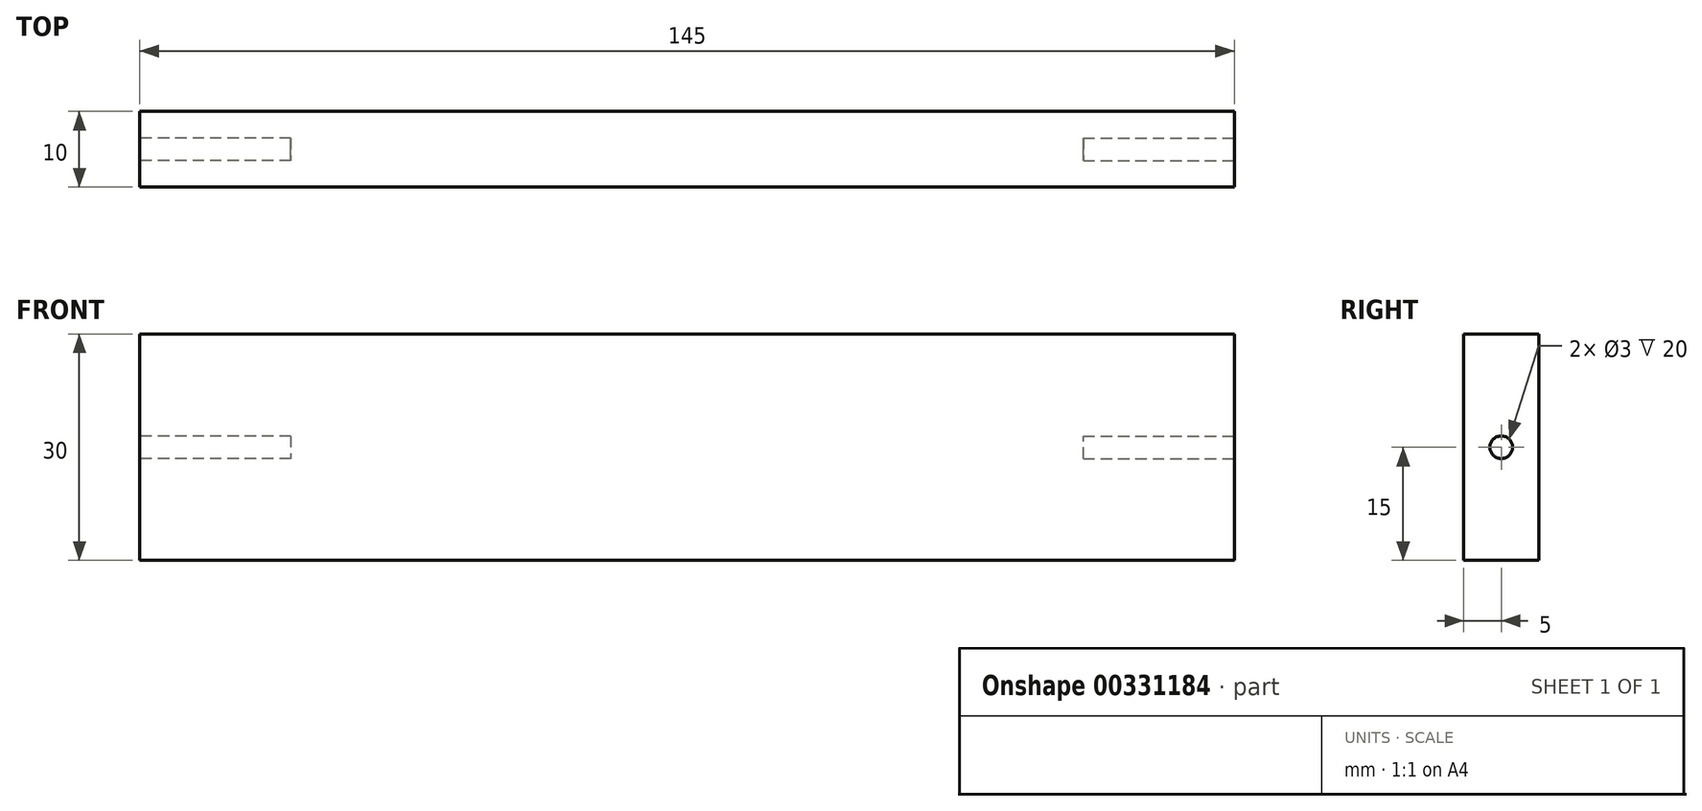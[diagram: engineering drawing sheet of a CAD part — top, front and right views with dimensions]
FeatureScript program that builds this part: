
annotation { "Feature Type Name" : "Feature", "Feature Type Description" : "" }
export const myFeature = defineFeature(function(context is Context, id is Id, definition is map)
    precondition{}
    {
        {
            var Q0;
            Q0=qCreatedBy(makeId("Front.planeOp"),FACE);
            var sketch = newSketch(context, id + "F0", { "sketchPlane" : qUnion([Q0])});
            skLineSegment(sketch, "E0.bottom", {"start": v(72.5, 15) * mm, "end": v(-72.5, 15) * mm});
            skLineSegment(sketch, "E0.top", {"start": v(72.5, -15) * mm, "end": v(-72.5, -15) * mm});
            skLineSegment(sketch, "E0.left", {"start": v(72.5, 15) * mm, "end": v(72.5, -15) * mm});
            skLineSegment(sketch, "E0.right", {"start": v(-72.5, 15) * mm, "end": v(-72.5, -15) * mm});
            skPoint(sketch, "E0.middle", {"position": v(0, 0) * mm});
            skSolve(sketch);
        }
        {
            var Q0;
            Q0=makeQuery(id+"F0.imprint","IMPRINT",FACE,{"disambiguationData":[TD([[makeQuery(id+"F0.imprint","IMPRINT",EDGE,{"derivedFrom":sQuery(id+"F0.wireOp",EDGE,"E0.bottom")}),1.0]])]});
            extrude(context, id + "F1", {"entities" : qUnion([Q0]), "depth" : 10 * mm});
        }
        {
            var Q0;
            Q0=makeQuery(id+"F1.opExtrude","SWEPT_FACE",FACE,{"disambiguationData":[OSD([sQuery(id+"F0.wireOp",EDGE,"E0.right")])]});
            var sketch = newSketch(context, id + "F2", { "sketchPlane" : qUnion([Q0])});
            skPoint(sketch, "E1", {"position": v(5, 0) * mm});
            skCircle(sketch, "E2", {"center": v(5, 0) * mm, "radius": 1.5 * mm});
            skPoint(sketch, "E3.orphan", {"position": v(0, 0) * mm});
            skPoint(sketch, "E4.orphan", {"position": v(10, 0) * mm});
            skSolve(sketch);
        }
        {
            var Q0;
            Q0 = qSketchRegion(id + "F2", true);
            extrude(context, id + "F3", {"entities" : qUnion([Q0]), "operationType" : NewBodyOperationType.REMOVE, "oppositeDirection" : true, "depth" : 20 * mm});
        }
        {
            var Q0;
            Q0=makeQuery(id+"F1.opExtrude","SWEPT_FACE",FACE,{"disambiguationData":[OSD([sQuery(id+"F0.wireOp",EDGE,"E0.left")])]});
            var sketch = newSketch(context, id + "F4", { "sketchPlane" : qUnion([Q0])});
            skPoint(sketch, "E5", {"position": v(-5, 0) * mm});
            skCircle(sketch, "E6", {"center": v(-5, 0) * mm, "radius": 1.5 * mm});
            skPoint(sketch, "E7.orphan", {"position": v(-10, 0) * mm});
            skPoint(sketch, "E8.orphan", {"position": v(0, 0) * mm});
            skSolve(sketch);
        }
        {
            var Q0;
            Q0 = qSketchRegion(id + "F4", true);
            extrude(context, id + "F5", {"entities" : qUnion([Q0]), "operationType" : NewBodyOperationType.REMOVE, "oppositeDirection" : true, "depth" : 20 * mm});
        }
    });
